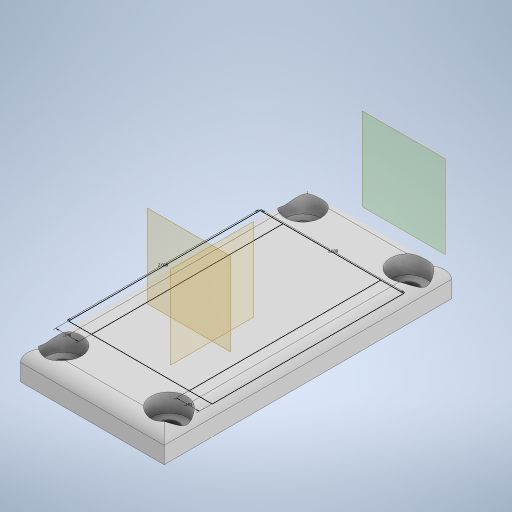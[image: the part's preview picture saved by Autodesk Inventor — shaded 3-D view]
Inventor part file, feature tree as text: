
AUTODESK INVENTOR PART (.ipt)
format: ipt  version: 2024.1 (Build 281209000, 209)  size: 381,952 bytes
history: native  units: in
note: dims shown in document units (in); Inventor stores cm internally (conversion verified against a paired STEP export)
features: sketch x7, extrude x5, plane x3, hole x2, projected_geometry x2, fillet x1
ambient origin geometry x8: Origin, YZ Plane, XZ Plane, XY Plane, X Axis, Y Axis, Z Axis, Center Point
bodies: Solid1 (feature_tree)
feature tree (20):
  extrude  "Extrusion2"  Depth=2.0in
  plane  "Work Plane1"
  plane  "Work Plane2"
  plane  "Work Plane3"
  extrude  "Extrusion3"  Depth=0.24in
  extrude  "Extrusion4"  Depth=0.5in TaperAngle=0.0deg
  extrude  "Extrusion5"  Depth=0.62in
  sketch  "Sketch6"  dims[d18=0.5in d19=0.0in d20=0.62in]
  hole  "Hole2"  [1 undecoded]
  hole  "Hole3"  [1 undecoded]
  fillet  "Fillet1"  Radius=0.1in
  extrude  "Extrusion6"  Depth=0.25in
  sketch  "Sketch3"  dims[d0=1.5in d1=2.0in]
  projected_geometry  "Projected Loop1"
  sketch  "Sketch4"  dims[d2=0.24in d3=0.24in]
  projected_geometry  "Projected Loop2"
  sketch  "Sketch5"  dims[d6=0.2in d7=0.0in d16=0.5in d17=0.0in]
  sketch  "Sketch7"  dims[d21=2.02in d22=0.5in]
  sketch  "Sketch8"  dims[d23=1.75in d24=0.5in d25=0.1in d26=0.0in]
  sketch  "Sketch9"  dims[d27=0.2in d28=0.25in d29=0.2in d30=0.25in d31=0.2in d32=0.25in d33=0.2in d34=0.1495in d35=0.75in d36=0.375in d37=0.25in d38=0.5635in d39=1.0in d40=0.8108in d41=0.201in d42=0.38in d43=0.375in d44=0.19in d45=0.5635in d46=1.0in d47=0.8108in d48=0.125in d49=0.17in d50=0.17in d51=0.17in d52=0.2in d53=0.3in d54=0.2in d55=0.3in d56=0.2in d57=0.3in d58=1.0in d59=0.0in]
note: 2 required parameter values undecoded (feature->parameter linkage not recoverable at this tier; creation-order binding heuristic only, values carry confidence <= 0.55)
